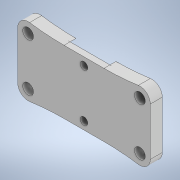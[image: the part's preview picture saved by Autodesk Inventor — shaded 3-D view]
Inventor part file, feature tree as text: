
AUTODESK INVENTOR PART (.ipt)
format: ipt  version: 2022 (Build 260153070, 153G)  size: 163,840 bytes
history: native  units: mm
features: extrude x2, sketch x1
ambient origin geometry x8: Origin, YZ Plane, XZ Plane, XY Plane, X Axis, Y Axis, Z Axis, Center Point
bodies: Solid1 (feature_tree)
feature tree (3):
  sketch  "Sketch1"  dims[d0=1.9mm d1=1.9mm d2=12.0mm d3=1.95mm d4=1.95mm d5=5.0mm d6=5.0mm d7=2.7mm d8=14.0mm d9=14.0mm d10=1.25mm d11=10.0mm d12=10.0mm d13=1.5mm d14=0.0mm d15=1.5mm d16=0.0mm]
  extrude  "Extrusion1"  Depth=1.5mm
  extrude  "Extrusion2"  Depth=1.5mm
